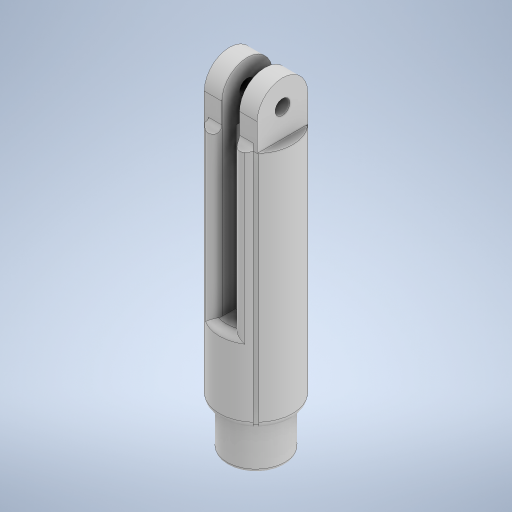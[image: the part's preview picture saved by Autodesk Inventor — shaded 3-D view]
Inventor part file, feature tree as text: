
AUTODESK INVENTOR PART (.ipt)
format: ipt  version: 2024.2 (Build 282272000, 272)  size: 432,128 bytes
history: native  units: mm
features: extrude x6, sketch x6, fillet x4, pattern_circular x1
ambient origin geometry x8: Origin, YZ Plane, XZ Plane, XY Plane, X Axis, Y Axis, Z Axis, Center Point
bodies: Solid1 (feature_tree)
feature tree (17):
  extrude  "Extrusion1"  Depth=80.0mm TaperAngle=0.0deg
  extrude  "Extrusion2"  Depth=5.0mm
  extrude  "Extrusion4"  Depth=15.0mm TaperAngle=0.0deg
  extrude  "Extrusion9"  TaperAngle=120.0deg  [1 undecoded]
  extrude  "Extrusion10"  TaperAngle=0.0deg  [1 undecoded]
  pattern_circular  "Circular Pattern2"  [2 undecoded]
  fillet  "Fillet4"  [1 undecoded]
  fillet  "Fillet5"  Radius=1.2mm
  extrude  "Extrusion11"  Depth=2.0mm
  fillet  "Fillet6"  Radius=2.0mm
  fillet  "Fillet7"  Radius=9.0mm
  sketch  "Sketch1"  dims[d0=20.75mm d1=80.0mm d2=0.0mm]
  sketch  "Sketch2"  dims[d3=5.0mm d4=5.0mm]
  sketch  "Sketch4"  dims[d5=5.0mm d6=15.0mm d7=0.0mm]
  sketch  "Sketch9"  dims[d12=8.0mm d13=120.0deg]
  sketch  "Sketch10"  dims[d14=120.0deg d17=0.0mm d18=0.0mm]
  sketch  "Sketch11"  dims[d36=4.2mm d37=0.0mm d38=0.0mm d41=45.0deg d42=1.2mm d43=0.6mm d44=2.0mm d45=9.0mm d46=16.5mm d47=22.0mm d48=12.0mm d49=0.0mm d50=40.0mm d51=360.0deg d53=2.0mm d54=1.0mm d55=5.0mm d56=45.0mm d57=0.0mm d58=0.0mm d59=2.0mm d60=2.0mm d29=0.5mm d30=0.872665mm d31=0.5mm d32=0.872665mm]
note: 5 required parameter values undecoded (feature->parameter linkage not recoverable at this tier; creation-order binding heuristic only, values carry confidence <= 0.55)
